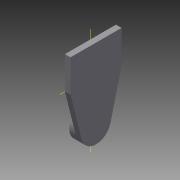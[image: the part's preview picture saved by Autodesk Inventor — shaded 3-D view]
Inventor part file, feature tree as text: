
AUTODESK INVENTOR PART (.ipt)
format: ipt  version: 2015 (Build 190159000, 159)  size: 88,064 bytes
history: native  units: mm
features: extrude x2, sketch x2
ambient origin geometry x8: Origin, YZ Plane, XZ Plane, XY Plane, X Axis, Y Axis, Z Axis, Center Point
bodies: Solid1 (feature_tree)
feature tree (4):
  extrude  "Extrusion1"  Depth=55.0mm
  extrude  "Extrusion2"  Depth=16.0mm
  sketch  "Sketch1"  dims[d0=55.0mm d1=35.0mm]
  sketch  "Sketch2"  dims[d2=18.0mm d3=16.0mm d4=60.0mm d5=6.0mm d6=0.0mm d7=7.0mm d8=0.0mm]
